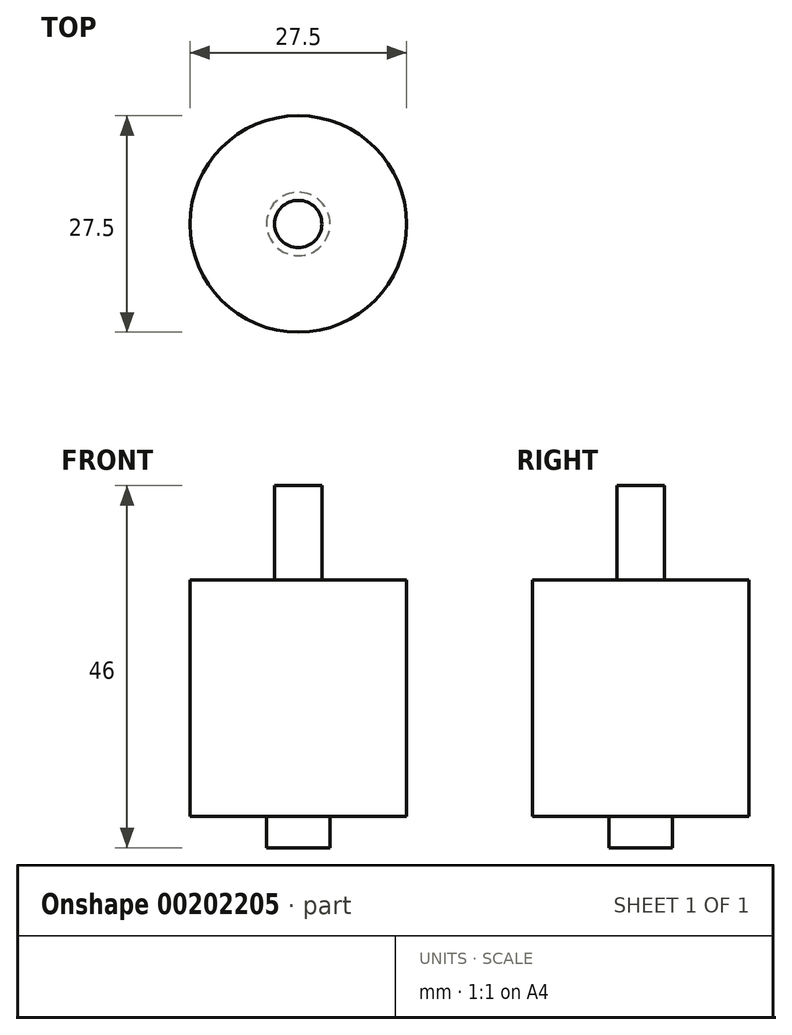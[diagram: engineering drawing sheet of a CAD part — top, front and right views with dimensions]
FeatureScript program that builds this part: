
annotation { "Feature Type Name" : "Feature", "Feature Type Description" : "" }
export const myFeature = defineFeature(function(context is Context, id is Id, definition is map)
    precondition{}
    {
        {
            var Q0;
            Q0=qCreatedBy(makeId("Top.planeOp"),FACE);
            var sketch = newSketch(context, id + "F0", { "sketchPlane" : qUnion([Q0])});
            skCircle(sketch, "E0", {"center": v(0, 0) * mm, "radius": 4.03 * mm});
            skSolve(sketch);
        }
        {
            var Q0;
            Q0=qSketchRegion(id+"F0",true);
            var Q1;
            Q1=qSketchRegion(id+"F2",true);
            extrude(context, id + "F1", {"entities" : qUnion([Q0, Q1]), "depth" : 4 * mm});
        }
        {
            var Q0;
            Q0=makeQuery(id+"F1.opExtrude","CAP_FACE",FACE,{"disambiguationData":[OSD([sQuery(id+"F0.wireOp",EDGE,"E0")])],"isStart":false});
            var sketch = newSketch(context, id + "F2", { "sketchPlane" : qUnion([Q0])});
            skCircle(sketch, "E1", {"center": v(0, 0) * mm, "radius": 13.75 * mm});
            skSolve(sketch);
        }
        {
            var Q0;
            Q0=qSketchRegion(id+"F2",true);
            extrude(context, id + "F3", {"entities" : qUnion([Q0]), "operationType" : NewBodyOperationType.ADD, "depth" : 30 * mm});
        }
        {
            var Q0;
            Q0=makeQuery(id+"F3.opExtrude","CAP_FACE",FACE,{"disambiguationData":[OSD([sQuery(id+"F2.wireOp",EDGE,"E1")])],"isStart":false});
            var sketch = newSketch(context, id + "F4", { "sketchPlane" : qUnion([Q0])});
            skCircle(sketch, "E2", {"center": v(0, 0) * mm, "radius": 3 * mm});
            skSolve(sketch);
        }
        {
            var Q0;
            Q0=qSketchRegion(id+"F4",true);
            extrude(context, id + "F5", {"entities" : qUnion([Q0]), "operationType" : NewBodyOperationType.ADD, "depth" : 12 * mm});
        }
    });
